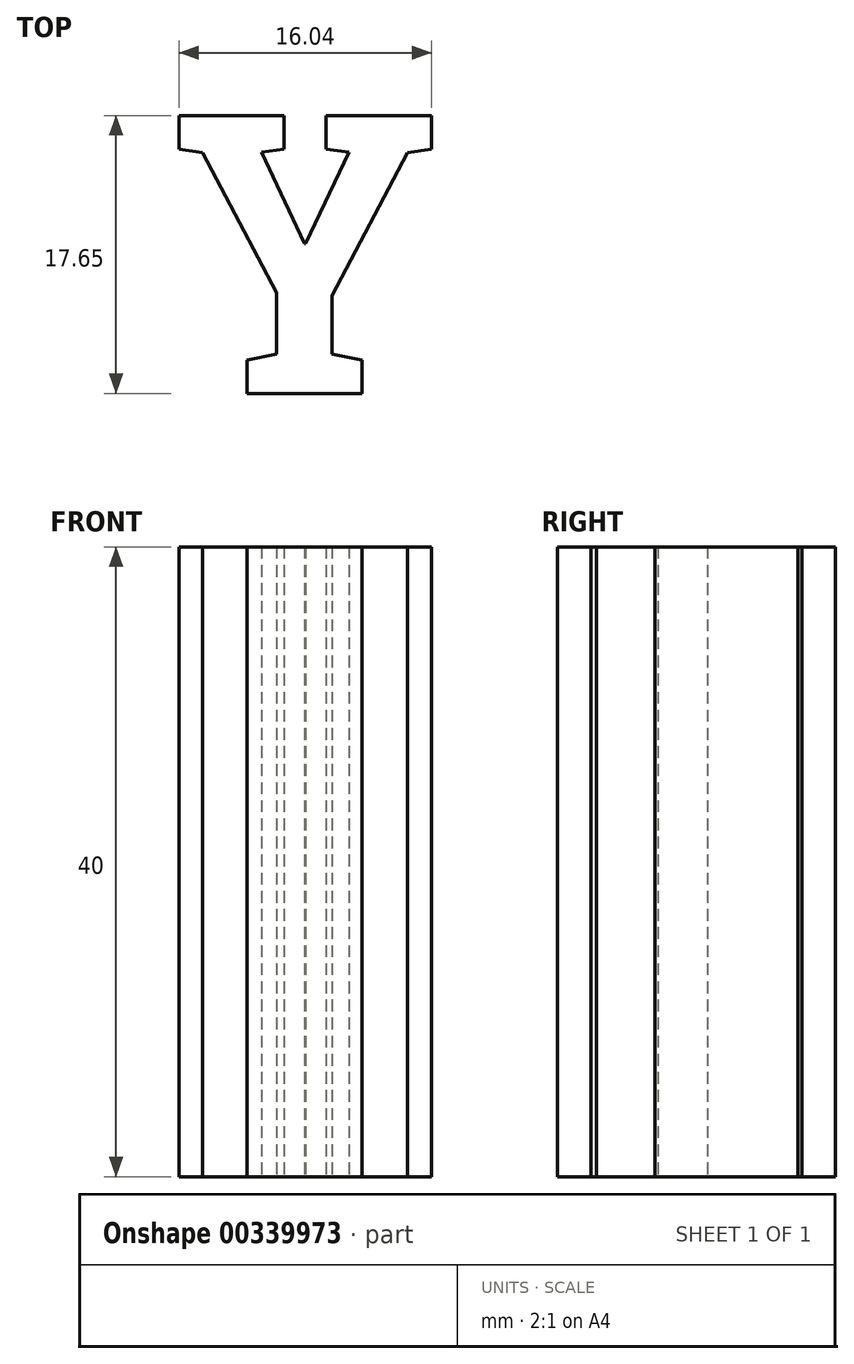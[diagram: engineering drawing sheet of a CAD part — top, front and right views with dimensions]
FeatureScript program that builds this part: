
annotation { "Feature Type Name" : "Feature", "Feature Type Description" : "" }
export const myFeature = defineFeature(function(context is Context, id is Id, definition is map)
    precondition{}
    {
        {
            var Q0;
            Q0=qCreatedBy(makeId("Top.planeOp"),FACE);
            var sketch = newSketch(context, id + "F0", { "sketchPlane" : qUnion([Q0])});
            skText(sketch, "E0", { "text": "Y", "fontName": "RobotoSlab-Bold.ttf"});
            const initialGuessF0  = {"E0": [-0.01162, -0.00793, 1, 0, 0.01788]};
            skSetInitialGuess(sketch, initialGuessF0);
            skSolve(sketch);
        }
        {
            var Q0;
            Q0 = qSketchRegion(id + "F0", true);
            extrude(context, id + "F1", {"entities" : qUnion([Q0]), "depth" : 40 * mm});
        }
    });
